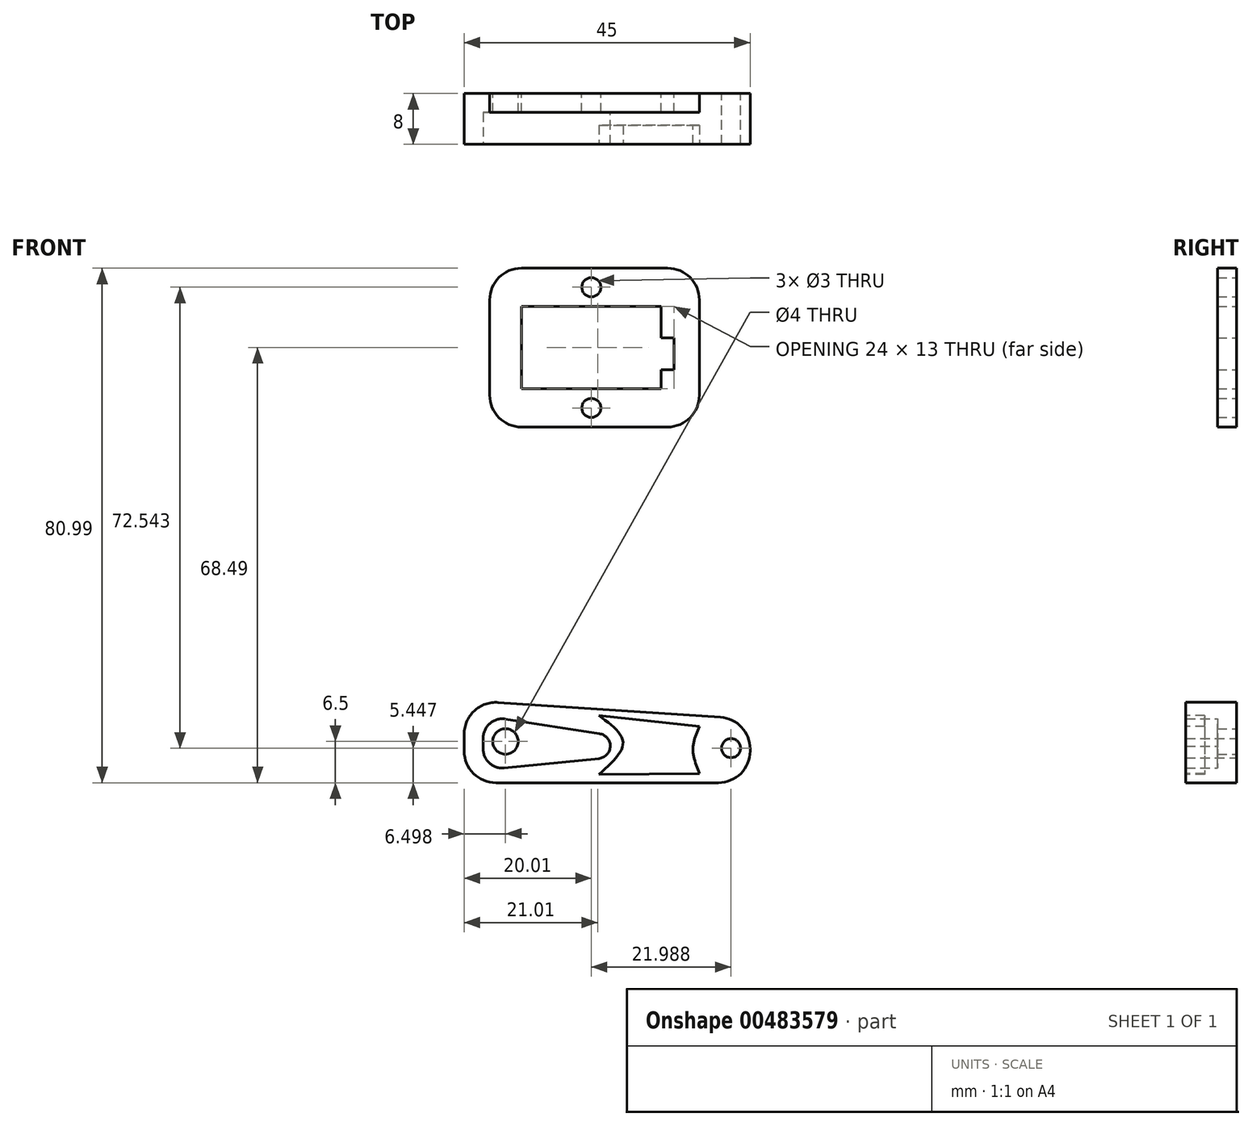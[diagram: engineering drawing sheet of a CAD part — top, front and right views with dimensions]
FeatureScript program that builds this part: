
annotation { "Feature Type Name" : "Feature", "Feature Type Description" : "" }
export const myFeature = defineFeature(function(context is Context, id is Id, definition is map)
    precondition{}
    {
        {
            var Q0;
            Q0=qCreatedBy(makeId("Front.planeOp"),FACE);
            var sketch = newSketch(context, id + "F0", { "sketchPlane" : qUnion([Q0])});
            skLineSegment(sketch, "E0", {"start": v(-37.01, -10) * mm, "end": v(7.99, -10) * mm});
            skLineSegment(sketch, "E1", {"start": v(7.99, -10) * mm, "end": v(7.99, 0) * mm});
            skLineSegment(sketch, "E2", {"start": v(-37.01, -10) * mm, "end": v(-37.01, 3) * mm});
            skLineSegment(sketch, "E3", {"start": v(-37.01, 3) * mm, "end": v(7.99, 0) * mm});
            skCircle(sketch, "E4", {"center": v(4.99, -4.55) * mm, "radius": 1.5 * mm});
            skPoint(sketch, "E5.endSnap0", {"position": v(-37.01, -3.5) * mm});
            skCircle(sketch, "E6", {"center": v(-30.51, -3.5) * mm, "radius": 2 * mm});
            skSolve(sketch);
        }
        {
            var Q0;
            Q0 = qSketchRegion(id + "F0", true);
            extrude(context, id + "F1", {"entities" : qUnion([Q0]), "depth" : 8 * mm});
        }
        {
            var Q0;
            Q0=makeQuery(id+"F1.opExtrude","SWEPT_EDGE",EDGE,{"disambiguationData":[OSD([sQuery(id+"F0.wireOp",EDGE,"E1"),sQuery(id+"F0.wireOp",EDGE,"E3")])]});
            var Q1;
            Q1=makeQuery(id+"F1.opExtrude","SWEPT_EDGE",EDGE,{"disambiguationData":[OSD([sQuery(id+"F0.wireOp",EDGE,"E0"),sQuery(id+"F0.wireOp",EDGE,"E1")])]});
            fillet(context, id + "F2", {"entities" : qUnion([Q0, Q1]), "radius" : 5 * mm, "tangentPropagation" : true, "allowEdgeOverflow" : false});
        }
        {
            var Q0;
            Q0=makeQuery(id+"F1.opExtrude","SWEPT_EDGE",EDGE,{"disambiguationData":[OSD([sQuery(id+"F0.wireOp",EDGE,"E2"),sQuery(id+"F0.wireOp",EDGE,"E3")])]});
            var Q1;
            Q1=makeQuery(id+"F1.opExtrude","SWEPT_EDGE",EDGE,{"disambiguationData":[OSD([sQuery(id+"F0.wireOp",EDGE,"E0"),sQuery(id+"F0.wireOp",EDGE,"E2")])]});
            fillet(context, id + "F3", {"entities" : qUnion([Q0, Q1]), "radius" : 5 * mm, "tangentPropagation" : true, "allowEdgeOverflow" : false});
        }
        {
            var Q0;
            Q0=makeQuery(id+"F1.opExtrude","CAP_FACE",FACE,{"disambiguationData":[OSD([sQuery(id+"F0.wireOp",EDGE,"E0"),sQuery(id+"F0.wireOp",EDGE,"E1"),sQuery(id+"F0.wireOp",EDGE,"E2"),sQuery(id+"F0.wireOp",EDGE,"E3"),sQuery(id+"F0.wireOp",EDGE,"E4"),sQuery(id+"F0.wireOp",EDGE,"E6")])],"isStart":false});
            var sketch = newSketch(context, id + "F4", { "sketchPlane" : qUnion([Q0])});
            skLineSegment(sketch, "E7", {"start": v(-14.01, -6) * mm, "end": v(-14.01, -2.53) * mm});
            skLineSegment(sketch, "E8", {"start": v(-14.01, -2.53) * mm, "end": v(-34.01, 0.57) * mm});
            skLineSegment(sketch, "E9", {"start": v(-34.01, -8) * mm, "end": v(-14.01, -6) * mm});
            skLineSegment(sketch, "E10", {"start": v(-34.01, 0.57) * mm, "end": v(-34.01, -8) * mm});
            skSolve(sketch);
        }
        {
            var Q0;
            Q0 = qSketchRegion(id + "F4", true);
            extrude(context, id + "F5", {"entities" : qUnion([Q0]), "operationType" : NewBodyOperationType.REMOVE, "oppositeDirection" : true, "depth" : 5 * mm});
        }
        {
            var Q0;
            Q0=makeQuery(id+"F5.boolean.opBoolean","COPY",EDGE,{"derivedFrom":makeQuery(id+"F5.opExtrude","SWEPT_EDGE",EDGE,{"disambiguationData":[OSD([sQuery(id+"F4.wireOp",EDGE,"E8"),sQuery(id+"F4.wireOp",EDGE,"E10")])]})});
            var Q1;
            Q1=makeQuery(id+"F5.boolean.opBoolean","COPY",EDGE,{"derivedFrom":makeQuery(id+"F5.opExtrude","SWEPT_EDGE",EDGE,{"disambiguationData":[OSD([sQuery(id+"F4.wireOp",EDGE,"E9"),sQuery(id+"F4.wireOp",EDGE,"E10")])]})});
            fillet(context, id + "F6", {"entities" : qUnion([Q0, Q1]), "radius" : 3 * mm, "tangentPropagation" : true, "allowEdgeOverflow" : false});
        }
        {
            var Q0;
            Q0=makeQuery(id+"F5.boolean.opBoolean","COPY",EDGE,{"derivedFrom":makeQuery(id+"F5.opExtrude","SWEPT_EDGE",EDGE,{"disambiguationData":[OSD([sQuery(id+"F4.wireOp",EDGE,"E7"),sQuery(id+"F4.wireOp",EDGE,"E8")])]})});
            var Q1;
            Q1=makeQuery(id+"F5.boolean.opBoolean","COPY",EDGE,{"derivedFrom":makeQuery(id+"F5.opExtrude","SWEPT_EDGE",EDGE,{"disambiguationData":[OSD([sQuery(id+"F4.wireOp",EDGE,"E7"),sQuery(id+"F4.wireOp",EDGE,"E9")])]})});
            fillet(context, id + "F7", {"entities" : qUnion([Q0, Q1]), "radius" : 2 * mm, "tangentPropagation" : true, "allowEdgeOverflow" : false});
        }
        {
            var Q0;
            Q0=makeQuery(id+"F1.opExtrude","CAP_FACE",FACE,{"disambiguationData":[OSD([sQuery(id+"F0.wireOp",EDGE,"E0"),sQuery(id+"F0.wireOp",EDGE,"E1"),sQuery(id+"F0.wireOp",EDGE,"E2"),sQuery(id+"F0.wireOp",EDGE,"E3"),sQuery(id+"F0.wireOp",EDGE,"E4"),sQuery(id+"F0.wireOp",EDGE,"E6")])],"isStart":false});
            var sketch = newSketch(context, id + "F8", { "sketchPlane" : qUnion([Q0])});
            skPoint(sketch, "E11.endSnap0", {"position": v(6.52, -8.54) * mm});
            skFitSpline(sketch, "E12", {"points": [v(-15.81, 0.59) * mm, v(-12.01, -3.67) * mm, v(-15.81, -8.67) * mm], "startDerivative": vector(11.5, -8.47) * mm, "endDerivative": vector(-11.32, -10.03) * mm});
            skFitSpline(sketch, "E13", {"points": [v(-0.01, -1.16) * mm, v(-1.01, -4.68) * mm, v(0, -8.54) * mm], "startDerivative": vector(-3.03, -7.1) * mm, "endDerivative": vector(3, -7.64) * mm});
            skLineSegment(sketch, "E14", {"start": v(-15.81, -8.67) * mm, "end": v(0, -8.54) * mm});
            skLineSegment(sketch, "E15", {"start": v(-0.01, -1.16) * mm, "end": v(-15.81, 0.59) * mm});
            skSolve(sketch);
        }
        {
            var Q0;
            Q0 = qSketchRegion(id + "F8", true);
            extrude(context, id + "F9", {"entities" : qUnion([Q0]), "operationType" : NewBodyOperationType.REMOVE, "oppositeDirection" : true, "depth" : 3 * mm});
        }
        {
            var Q0;
            Q0=qCreatedBy(makeId("Front.planeOp"),FACE);
            var sketch = newSketch(context, id + "F10", { "sketchPlane" : qUnion([Q0])});
            skLineSegment(sketch, "E16", {"start": v(-33, 45.99) * mm, "end": v(0, 45.99) * mm});
            skLineSegment(sketch, "E17", {"start": v(0, 45.99) * mm, "end": v(0, 70.99) * mm});
            skLineSegment(sketch, "E18", {"start": v(0, 70.99) * mm, "end": v(-33, 70.99) * mm});
            skLineSegment(sketch, "E19", {"start": v(-33, 70.99) * mm, "end": v(-33, 45.99) * mm});
            skLineSegment(sketch, "E20", {"start": v(-28, 51.99) * mm, "end": v(-28, 64.99) * mm});
            skLineSegment(sketch, "E21", {"start": v(-28, 51.99) * mm, "end": v(-6, 51.99) * mm});
            skLineSegment(sketch, "E22", {"start": v(-6, 51.99) * mm, "end": v(-6, 54.99) * mm});
            skLineSegment(sketch, "E23", {"start": v(-6, 54.99) * mm, "end": v(-4, 54.99) * mm});
            skLineSegment(sketch, "E24", {"start": v(-4, 54.99) * mm, "end": v(-4, 59.99) * mm});
            skLineSegment(sketch, "E25", {"start": v(-4, 59.99) * mm, "end": v(-6, 59.99) * mm});
            skLineSegment(sketch, "E26", {"start": v(-6, 59.99) * mm, "end": v(-6, 64.99) * mm});
            skLineSegment(sketch, "E27", {"start": v(-6, 64.99) * mm, "end": v(-28, 64.99) * mm});
            skCircle(sketch, "E28", {"center": v(-17, 67.99) * mm, "radius": 1.5 * mm});
            skCircle(sketch, "E29", {"center": v(-17, 48.99) * mm, "radius": 1.5 * mm});
            skSolve(sketch);
        }
        {
            var Q0;
            Q0 = qSketchRegion(id + "F10", true);
            extrude(context, id + "F11", {"entities" : qUnion([Q0]), "depth" : 3 * mm});
        }
        {
            var Q0;
            Q0=makeQuery(id+"F11.opExtrude","SWEPT_EDGE",EDGE,{"disambiguationData":[OSD([sQuery(id+"F10.wireOp",EDGE,"E18"),sQuery(id+"F10.wireOp",EDGE,"E19")])]});
            var Q1;
            Q1=makeQuery(id+"F11.opExtrude","SWEPT_EDGE",EDGE,{"disambiguationData":[OSD([sQuery(id+"F10.wireOp",EDGE,"E16"),sQuery(id+"F10.wireOp",EDGE,"E19")])]});
            var Q2;
            Q2=makeQuery(id+"F11.opExtrude","SWEPT_EDGE",EDGE,{"disambiguationData":[OSD([sQuery(id+"F10.wireOp",EDGE,"E16"),sQuery(id+"F10.wireOp",EDGE,"E17")])]});
            var Q3;
            Q3=makeQuery(id+"F11.opExtrude","SWEPT_EDGE",EDGE,{"disambiguationData":[OSD([sQuery(id+"F10.wireOp",EDGE,"E17"),sQuery(id+"F10.wireOp",EDGE,"E18")])]});
            fillet(context, id + "F12", {"entities" : qUnion([Q0, Q1, Q2, Q3]), "radius" : 5 * mm, "tangentPropagation" : true, "allowEdgeOverflow" : false});
        }
    });
